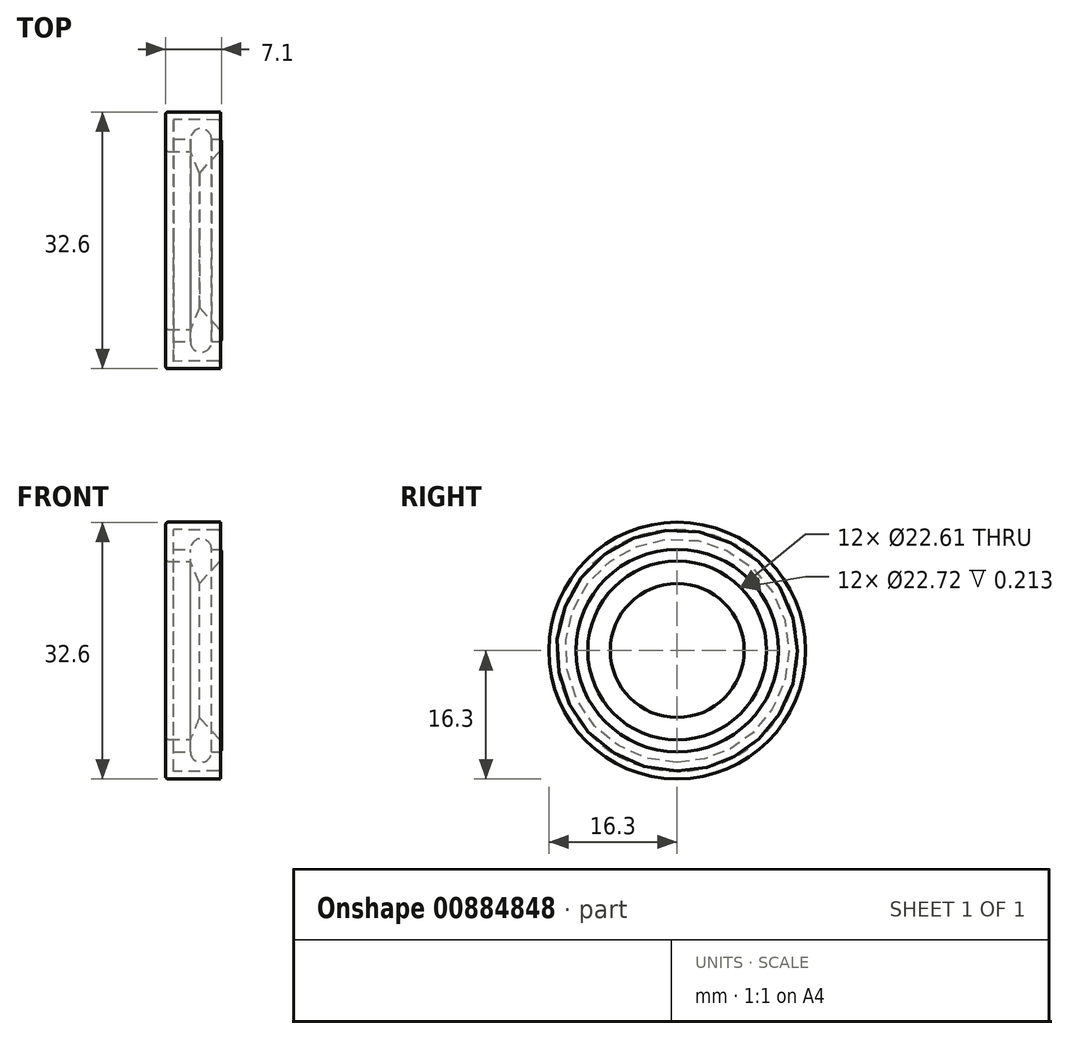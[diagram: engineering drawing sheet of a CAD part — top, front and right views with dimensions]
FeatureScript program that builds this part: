
annotation { "Feature Type Name" : "Feature", "Feature Type Description" : "" }
export const myFeature = defineFeature(function(context is Context, id is Id, definition is map)
    precondition{}
    {
        {
            var Q0;
            Q0=qCreatedBy(makeId("Front.planeOp"),FACE);
            var sketch = newSketch(context, id + "F0", { "sketchPlane" : qUnion([Q0])});
            skLineSegment(sketch, "E0", {"start": v(0, 0) * mm, "end": v(-25.44, 0) * mm, "construction": true});
            skLineSegment(sketch, "E1", {"start": v(7, 16.3) * mm, "end": v(0.3, 16.3) * mm});
            skLineSegment(sketch, "E2", {"start": v(0, 16) * mm, "end": v(0, 11.6) * mm});
            skLineSegment(sketch, "E3", {"start": v(0.3, 11.3) * mm, "end": v(3.14, 11.3) * mm});
            skLineSegment(sketch, "E4", {"start": v(6.89, 11.36) * mm, "end": v(7.1, 11.36) * mm});
            skLineSegment(sketch, "E5", {"start": v(7.1, 11.36) * mm, "end": v(7.1, 12.56) * mm});
            skLineSegment(sketch, "E6", {"start": v(6.8, 12.86) * mm, "end": v(5.83, 12.86) * mm});
            skArc(sketch, "E7", {"start": v(5.83, 12.86) * mm, "mid": v(4.48, 14.2) * mm, "end": v(3.14, 12.86) * mm});
            skLineSegment(sketch, "E8", {"start": v(3.14, 12.86) * mm, "end": v(1, 12.86) * mm});
            skLineSegment(sketch, "E9", {"start": v(1, 12.86) * mm, "end": v(1, 15.36) * mm});
            skLineSegment(sketch, "E10", {"start": v(1, 15.36) * mm, "end": v(6.7, 15.3) * mm});
            skLineSegment(sketch, "E11", {"start": v(7, 15.6) * mm, "end": v(7, 16.3) * mm});
            skLineSegment(sketch, "E12", {"start": v(3.14, 11.3) * mm, "end": v(4.29, 8.5) * mm});
            skLineSegment(sketch, "E13", {"start": v(4.29, 8.5) * mm, "end": v(6.89, 11.36) * mm});
            skPoint(sketch, "E14.visualSharp", {"position": v(0, 16.3) * mm});
            skArc(sketch, "E14.filletArc", {"start": v(0.3, 16.3) * mm, "mid": v(0.09, 16.22) * mm, "end": v(0, 16) * mm});
            skPoint(sketch, "E15.visualSharp", {"position": v(0, 11.3) * mm});
            skArc(sketch, "E15.filletArc", {"start": v(0, 11.6) * mm, "mid": v(0.09, 11.4) * mm, "end": v(0.3, 11.3) * mm});
            skPoint(sketch, "E16.visualSharp", {"position": v(7, 15.3) * mm});
            skArc(sketch, "E16.filletArc", {"start": v(6.7, 15.3) * mm, "mid": v(6.91, 15.4) * mm, "end": v(7, 15.6) * mm});
            skPoint(sketch, "E17.visualSharp", {"position": v(7.1, 12.86) * mm});
            skArc(sketch, "E17.filletArc", {"start": v(7.1, 12.56) * mm, "mid": v(7.01, 12.77) * mm, "end": v(6.8, 12.86) * mm});
            skSolve(sketch);
        }
        {
            var Q0;
            Q0 = qSketchRegion(id + "F0", true);
            var Q1;
            Q1=sQuery(id+"F0.wireOp",EDGE,"E0");
            revolve(context, id + "F1", {"surfaceOperationType" : NewSurfaceOperationType.NEW, "entities" : qUnion([Q0]), "axis" : qUnion([Q1]), "revolveType" : RevolveType.FULL});
        }
    });
